# Revit family: BC_Aircalo_BORA-60-STD-Gauche_LOD400
name_source: partatom
category: Mechanical Equipment
revit_build: Autodesk Revit 2017 (Build: 20160720_1515(x64)
units: mm (PartAtom-declared; Revit-internal decimal feet)

## family parameters
Always vertical = No
Cut with Voids When Loaded = No
OmniClass Number = 23.75.70.17.27
OmniClass Title = Fan Coil Units
Part Type = Normal
Room Calculation Point = No
Round Connector Dimension = Use Diameter
Shared = No
Work Plane-Based = No

## types (2) — shared parameters
Body Material = Bora Fancoil Body Material
Connection Diameter = 13 mm  [stored 0.0426509 ft]
Dalle Staff Material = Bora Fancoil Body Material
Filter class = G3;G4
Foiler Material = Bora Fancoil Foiler Material
Galvanized = Galvanized
Grill Material = Bora Fancoil Grill Material
Insulation Material = Mousse polyuréthane ignifugé 20mm
Length Cassette = 595 mm  [stored 1.9521 ft]
Main Material = Acier galvanisé
Manufacturer = Aircalo
Manufacturer Product Link = http://aircalo.fr
Model = Bora Standard
Motor power absorbed = 100 W
New Air Diameter = 125 mm
Nominal Voltage = 230 V
Outlet Diameter = 16 mm  [stored 0.0524934 ft]
Overall Length = 865 mm  [stored 2.83793 ft]
Overall Width = 599 mm  [stored 1.96522 ft]
Second Diameter = 13 mm  [stored 0.0426509 ft]
Trap Material = Bora Fancoil Body Material
Valve-Body Material = Valve Body Material
Valve-Head Material = Valve Head Material
zero-valued in all types: Thin line THK

## per-type parameters (varying)
| type | Mass | Overall Height | Product Code |
| Bora 60 Standard - Hauteur 300mm | 27.00 kg | 300 mm | B1A |
| Bora 60 Standard - Hauteur 380mm | 30.00 kg | 380 mm | B3A |

note: [stored X ft] marks values corroborated as IEEE doubles in the binary element streams (Revit-internal decimal feet)

## geometry (parser evidence)
native form markers: Sweep x12
no freeform markers — native parametric forms only
